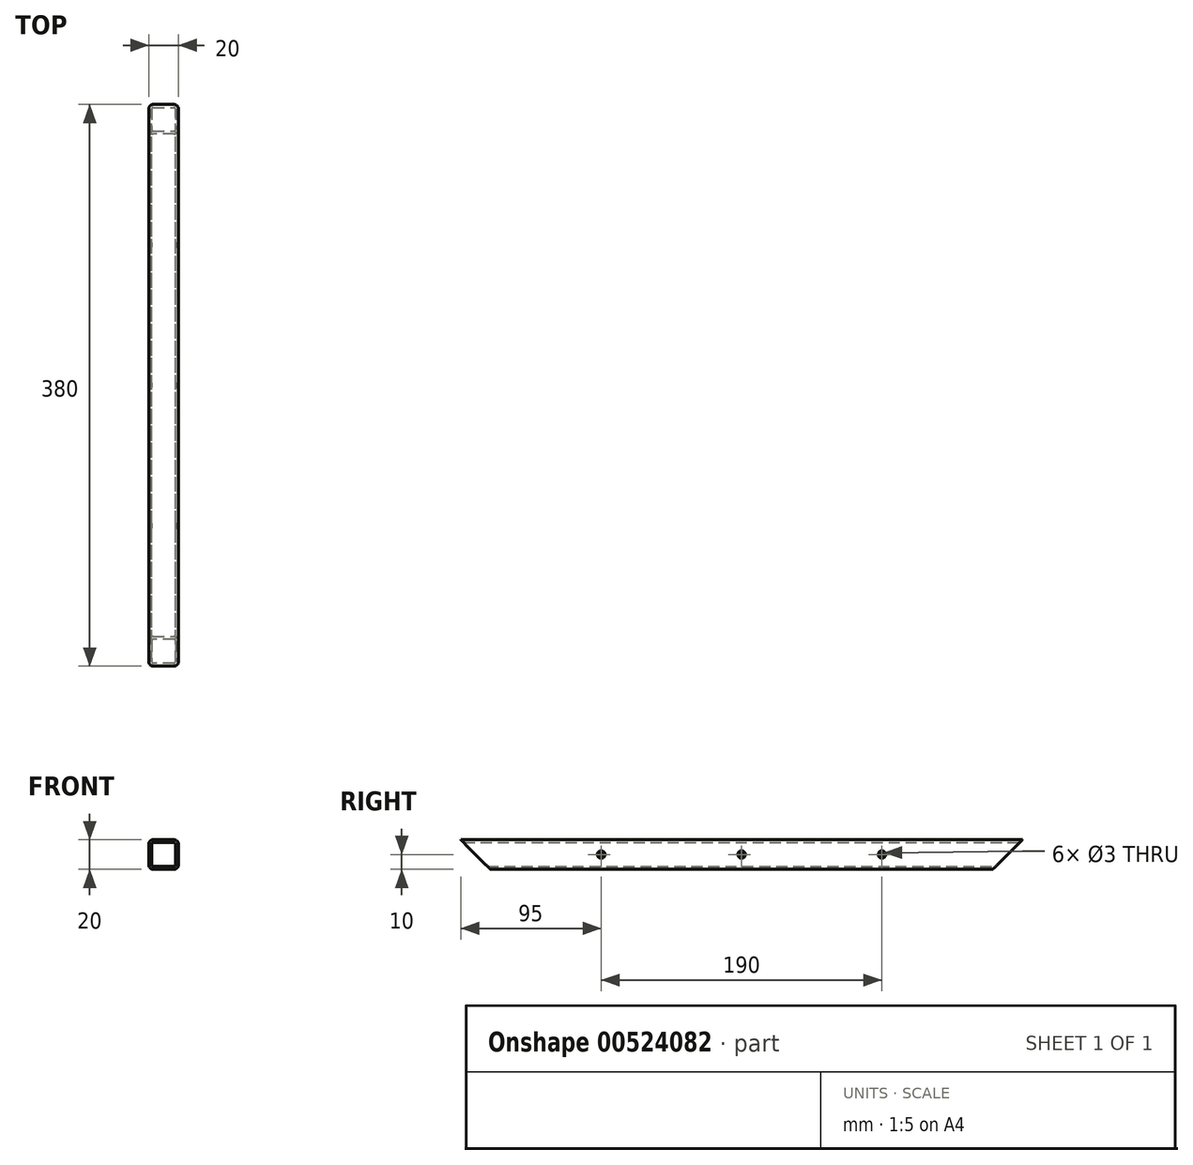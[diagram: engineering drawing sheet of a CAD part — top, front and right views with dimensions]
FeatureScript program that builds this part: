
annotation { "Feature Type Name" : "Feature", "Feature Type Description" : "" }
export const myFeature = defineFeature(function(context is Context, id is Id, definition is map)
    precondition{}
    {
        {
            assignVariable(context, id + "F0", {"name" : "R", "anyValue" : 3});
        }
        {
            assignVariable(context, id + "F1", {"name" : "W", "anyValue" : 2});
        }
        {
            var Q0;
            Q0=qCreatedBy(makeId("Front.planeOp"),FACE);
            var sketch = newSketch(context, id + "F2", { "sketchPlane" : qUnion([Q0])});
            skLineSegment(sketch, "E0.bottom", {"start": v(-10, 10) * mm, "end": v(10, 10) * mm});
            skLineSegment(sketch, "E0.top", {"start": v(-10, -10) * mm, "end": v(10, -10) * mm});
            skLineSegment(sketch, "E0.left", {"start": v(-10, 10) * mm, "end": v(-10, -10) * mm});
            skLineSegment(sketch, "E0.right", {"start": v(10, 10) * mm, "end": v(10, -10) * mm});
            skSolve(sketch);
        }
        {
            var Q0;
            Q0=qSketchRegion(id+"F2",true);
            extrude(context, id + "F3", {"entities" : qUnion([Q0]), "endBound" : BoundingType.SYMMETRIC, "depth" : 380 * mm, "offsetDistance" : 25 * mm});
        }
        {
            var Q0;
            Q0=makeQuery(id+"F3.opExtrude","SWEPT_EDGE",EDGE,{"disambiguationData":[OSD([sQuery(id+"F2.wireOp",EDGE,"E0.bottom"),sQuery(id+"F2.wireOp",EDGE,"E0.right")])]});
            var Q1;
            Q1=makeQuery(id+"F3.opExtrude","SWEPT_EDGE",EDGE,{"disambiguationData":[OSD([sQuery(id+"F2.wireOp",EDGE,"E0.bottom"),sQuery(id+"F2.wireOp",EDGE,"E0.left")])]});
            var Q2;
            Q2=makeQuery(id+"F3.opExtrude","SWEPT_EDGE",EDGE,{"disambiguationData":[OSD([sQuery(id+"F2.wireOp",EDGE,"E0.top"),sQuery(id+"F2.wireOp",EDGE,"E0.right")])]});
            var Q3;
            Q3=makeQuery(id+"F3.opExtrude","SWEPT_EDGE",EDGE,{"disambiguationData":[OSD([sQuery(id+"F2.wireOp",EDGE,"E0.top"),sQuery(id+"F2.wireOp",EDGE,"E0.left")])]});
            fillet(context, id + "F4", {"entities" : qUnion([Q0, Q1, Q2, Q3]), "radius" : (getVariable(context, 'R')) * mm, "tangentPropagation" : true, "allowEdgeOverflow" : false});
        }
        {
            var Q0;
            Q0=makeQuery(id+"F3.opExtrude","CAP_FACE",FACE,{"disambiguationData":[OSD([sQuery(id+"F2.wireOp",EDGE,"E0.bottom"),sQuery(id+"F2.wireOp",EDGE,"E0.top"),sQuery(id+"F2.wireOp",EDGE,"E0.left"),sQuery(id+"F2.wireOp",EDGE,"E0.right")])],"isStart":false});
            var Q1;
            Q1=makeQuery(id+"F3.opExtrude","CAP_FACE",FACE,{"disambiguationData":[OSD([sQuery(id+"F2.wireOp",EDGE,"E0.bottom"),sQuery(id+"F2.wireOp",EDGE,"E0.top"),sQuery(id+"F2.wireOp",EDGE,"E0.left"),sQuery(id+"F2.wireOp",EDGE,"E0.right")])],"isStart":true});
            shell(context, id + "F5", {"entities" : qUnion([Q0, Q1]), "thickness" : (getVariable(context, 'W')) * mm});
        }
        {
            var Q0;
            Q0=makeQuery(id+"F3.opExtrude","SWEPT_FACE",FACE,{"disambiguationData":[OSD([sQuery(id+"F2.wireOp",EDGE,"E0.left")])]});
            var sketch = newSketch(context, id + "F6", { "sketchPlane" : qUnion([Q0])});
            skLineSegment(sketch, "E1", {"start": v(-190, -10) * mm, "end": v(-170, -10) * mm});
            skLineSegment(sketch, "E2", {"start": v(-170, -10) * mm, "end": v(-190, 10) * mm});
            skLineSegment(sketch, "E3", {"start": v(-190, 10) * mm, "end": v(-190, -10) * mm});
            skSolve(sketch);
        }
        {
            var Q0;
            Q0=qSketchRegion(id+"F6",true);
            extrude(context, id + "F7", {"entities" : qUnion([Q0]), "operationType" : NewBodyOperationType.REMOVE, "endBound" : BoundingType.THROUGH_ALL, "oppositeDirection" : true, "depth" : 25 * mm, "offsetDistance" : 25 * mm});
        }
        {
            var Q0;
            Q0=makeQuery(id+"F3.opExtrude","SWEPT_FACE",FACE,{"disambiguationData":[OSD([sQuery(id+"F2.wireOp",EDGE,"E0.right")])]});
            var sketch = newSketch(context, id + "F8", { "sketchPlane" : qUnion([Q0])});
            skLineSegment(sketch, "E4.0", {"start": v(170, -10) * mm, "end": v(-190, -10) * mm, "construction": true});
            skLineSegment(sketch, "E4.1", {"start": v(-190, 10) * mm, "end": v(190, 10) * mm, "construction": true});
            skLineSegment(sketch, "E5", {"start": v(-170, -10) * mm, "end": v(-190, 10) * mm});
            skLineSegment(sketch, "E6", {"start": v(-190, -10) * mm, "end": v(-170, -10) * mm});
            skLineSegment(sketch, "E7", {"start": v(-190, 10) * mm, "end": v(-190, -10) * mm});
            skSolve(sketch);
        }
        {
            var Q0;
            Q0=qSketchRegion(id+"F8",true);
            extrude(context, id + "F9", {"entities" : qUnion([Q0]), "operationType" : NewBodyOperationType.REMOVE, "endBound" : BoundingType.THROUGH_ALL, "oppositeDirection" : true, "depth" : 25 * mm, "offsetDistance" : 25 * mm});
        }
        {
            var Q0;
            Q0=makeQuery(id+"F3.opExtrude","SWEPT_FACE",FACE,{"disambiguationData":[OSD([sQuery(id+"F2.wireOp",EDGE,"E0.right")])]});
            var sketch = newSketch(context, id + "F10", { "sketchPlane" : qUnion([Q0])});
            skPoint(sketch, "E8", {"position": v(95, 0) * mm});
            skPoint(sketch, "E9", {"position": v(0, 0) * mm});
            skPoint(sketch, "E10", {"position": v(-95, 0) * mm});
            skSolve(sketch);
        }
        {
            var Q0;
            Q0=sQuery(id+"F10.wireOp",VERTEX,"E8");
            var Q1;
            Q1=sQuery(id+"F10.wireOp",VERTEX,"E9");
            var Q2;
            Q2=sQuery(id+"F10.wireOp",VERTEX,"E10");
            var Q3;
            Q3=makeQuery(id+"F3.opExtrude","SWEPT_BODY",BODY,{"disambiguationData":[OSD([sQuery(id+"F2.wireOp",EDGE,"E0.bottom"),sQuery(id+"F2.wireOp",EDGE,"E0.top"),sQuery(id+"F2.wireOp",EDGE,"E0.left"),sQuery(id+"F2.wireOp",EDGE,"E0.right")])]});
            hole(context, id + "F11", {"style" : HoleStyle.C_SINK, "endStyle" : HoleEndStyle.THROUGH, "holeDiameter" : 3 * mm, "cSinkDiameter" : 5 * mm, "cSinkAngle" : 90 * degree, "isTappedThrough" : true, "tappedDepth" : 12 * mm, "tapClearance" : 3, "locations" : qUnion([Q0, Q1, Q2]), "scope" : qUnion([Q3])});
        }
    });
